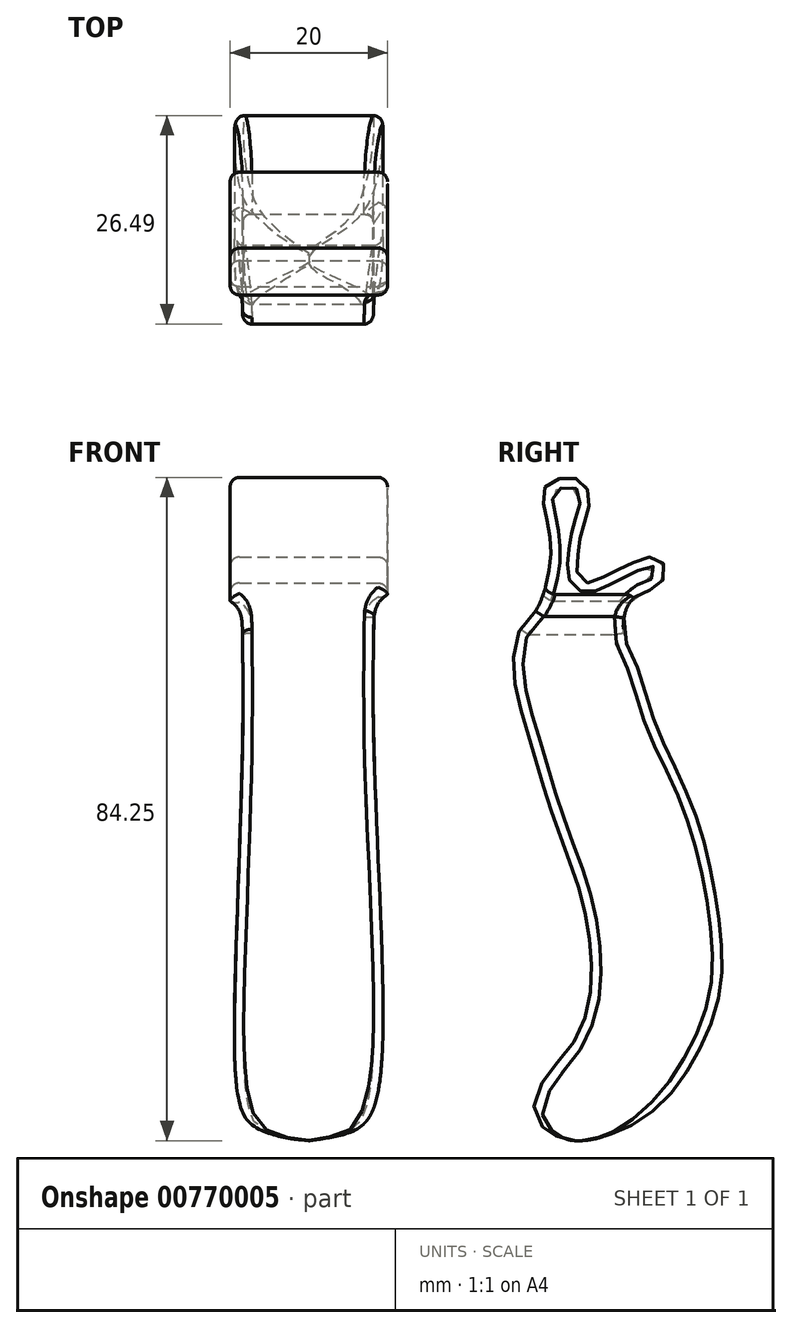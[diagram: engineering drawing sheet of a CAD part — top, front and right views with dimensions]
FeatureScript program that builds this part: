
annotation { "Feature Type Name" : "Feature", "Feature Type Description" : "" }
export const myFeature = defineFeature(function(context is Context, id is Id, definition is map)
    precondition{}
    {
        {
            var Q0;
            Q0=qCreatedBy(makeId("Right.planeOp"),FACE);
            var sketch = newSketch(context, id + "F0", { "sketchPlane" : qUnion([Q0])});
            skFitSpline(sketch, "E0", {"points": [v(-60.53, -63.1) * mm, v(-56.71, -65.93) * mm, v(-50.2, -65.08) * mm, v(-43.68, -60.7) * mm, v(-37.59, -49.79) * mm, v(-36.88, -40.01) * mm, v(-40.14, -24.57) * mm, v(-45.1, -13.38) * mm, v(-47.5, -5.88) * mm, v(-49.2, -1.49) * mm, v(-47.93, 2.76) * mm, v(-44.67, 4.46) * mm, v(-43.96, 6.73) * mm, v(-45.52, 8) * mm, v(-52.6, 5.03) * mm, v(-54.21, 4.8) * mm, v(-54.98, 5.6) * mm, v(-55.04, 8) * mm, v(-54.36, 11.9) * mm, v(-53.56, 14.68) * mm, v(-54, 17.09) * mm, v(-54.69, 17.77) * mm, v(-56.27, 18.1) * mm, v(-59.12, 16.97) * mm, v(-59.24, 14) * mm, v(-58.46, 8.04) * mm, v(-60.59, 0.82) * mm, v(-62.5, -1.45) * mm, v(-63.07, -7.54) * mm, v(-61.37, -14.34) * mm, v(-58.15, -24.94) * mm, v(-54.46, -35.66) * mm, v(-53.39, -46.97) * mm, v(-55.77, -54) * mm, v(-58.5, -57.21) * mm, v(-59.73, -59.21) * mm, v(-60.5, -61.4) * mm, v(-60.53, -63.1) * mm]});
            skSolve(sketch);
        }
        {
            var Q0;
            Q0=makeQuery(id+"F0.imprint","IMPRINT",FACE,{"disambiguationData":[TD([[makeQuery(id+"F0.imprint","IMPRINT",EDGE,{"derivedFrom":sQuery(id+"F0.wireOp",EDGE,"E0")}),1.0]])]});
            var Q1;
            Q1=sQuery(id+"F0.wireOp",EDGE,"E0");
            extrude(context, id + "F1", {"entities" : qUnion([Q0]), "surfaceEntities" : qUnion([Q1]), "depth" : 20 * mm, "offsetDistance" : 25 * mm});
        }
        {
            var Q0;
            Q0=qCreatedBy(makeId("Front.planeOp"),FACE);
            var sketch = newSketch(context, id + "F2", { "sketchPlane" : qUnion([Q0])});
            skFitSpline(sketch, "E1", {"points": [v(10.06, -66.14) * mm, v(16, -64.73) * mm, v(18.41, -61.47) * mm, v(19.4, -46.46) * mm, v(18.27, -16.71) * mm, v(18.27, 0.43) * mm], "startDerivative": vector(48.67, 6.61) * mm, "endDerivative": vector(1.2, 67.59) * mm});
            skFitSpline(sketch, "E2", {"points": [v(10.06, -66.14) * mm, v(7.19, -65.83) * mm, v(3.54, -64.62) * mm, v(1.45, -62.21) * mm, v(0.6, -46.94) * mm, v(1.55, -17.24) * mm, v(1.55, -1.83) * mm], "startDerivative": vector(-30.12, 2) * mm, "endDerivative": vector(-0.9, 66.05) * mm});
            skFitSpline(sketch, "E3", {"points": [v(1.55, -1.83) * mm, v(1.06, 1.34) * mm, v(-1.32, 3.19) * mm], "startDerivative": vector(0, 6.88) * mm, "endDerivative": vector(-5.8, 3.14) * mm});
            skFitSpline(sketch, "E4", {"points": [v(18.27, 0.43) * mm, v(18.86, 2.17) * mm, v(20.59, 3.66) * mm], "startDerivative": vector(0.77, 3.9) * mm, "endDerivative": vector(3.81, 2.6) * mm});
            skLineSegment(sketch, "E5", {"start": v(20.59, 3.66) * mm, "end": v(26.08, -16.44) * mm});
            skLineSegment(sketch, "E6", {"start": v(26.08, -16.44) * mm, "end": v(26.08, -49.43) * mm});
            skLineSegment(sketch, "E7", {"start": v(26.08, -49.43) * mm, "end": v(22.62, -70.4) * mm});
            skLineSegment(sketch, "E8", {"start": v(22.62, -70.4) * mm, "end": v(8.45, -72.78) * mm});
            skLineSegment(sketch, "E9", {"start": v(8.45, -72.78) * mm, "end": v(-14.42, -70.87) * mm});
            skLineSegment(sketch, "E10", {"start": v(-14.42, -70.87) * mm, "end": v(-9.9, -31.8) * mm});
            skLineSegment(sketch, "E11", {"start": v(-9.9, -31.8) * mm, "end": v(-1.32, 3.19) * mm});
            skSolve(sketch);
        }
        {
            var Q0;
            Q0=makeQuery(id+"F2.imprint","IMPRINT",FACE,{"disambiguationData":[TD([[makeQuery(id+"F2.imprint","IMPRINT",EDGE,{"derivedFrom":sQuery(id+"F2.wireOp",EDGE,"E1")}),-1.0]])]});
            extrude(context, id + "F3", {"entities" : qUnion([Q0]), "operationType" : NewBodyOperationType.REMOVE, "depth" : 106.6 * mm, "offsetDistance" : 25 * mm});
        }
        {
            var Q0;
            Q0=makeQuery(id+"F1.opExtrude","SWEPT_FACE",FACE,{"disambiguationData":[OSD([sQuery(id+"F0.wireOp",EDGE,"E0")])]});
            fillet(context, id + "F4", {"entities" : qUnion([Q0]), "radius" : 1.2 * mm, "tangentPropagation" : true, "allowEdgeOverflow" : false});
        }
    });
